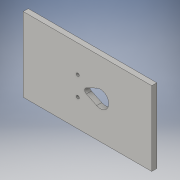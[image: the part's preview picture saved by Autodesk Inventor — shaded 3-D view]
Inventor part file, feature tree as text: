
AUTODESK INVENTOR PART (.ipt)
format: ipt  version: 2016 (Build 200138000, 138)  size: 111,616 bytes
history: native  units: in
note: dims shown in document units (in); Inventor stores cm internally (conversion verified against a paired STEP export)
features: extrude x1, sketch x1
ambient origin geometry x8: Origin, YZ Plane, XZ Plane, XY Plane, X Axis, Y Axis, Z Axis, Center Point
bodies: Solid1 (feature_tree)
feature tree (2):
  extrude  "Extrusion1"  Depth=0.18in
  sketch  "Sketch1"  dims[d7=0.5in d8=0.75in d11=0.135in d12=0.15in d13=0.053in d14=0.2925in d15=0.2925in d16=0.053in d17=0.053in d18=0.6in d19=0.2in d21=0.18in d22=0.0in]
